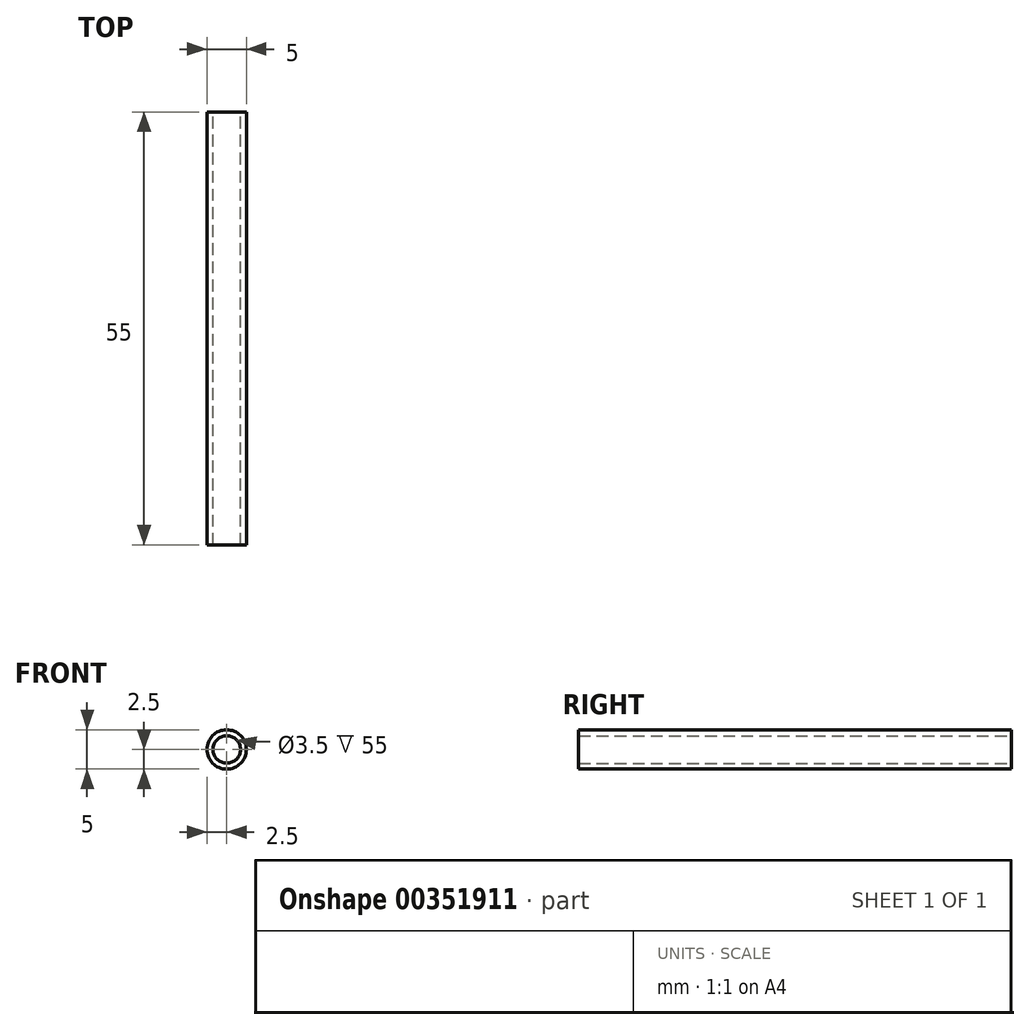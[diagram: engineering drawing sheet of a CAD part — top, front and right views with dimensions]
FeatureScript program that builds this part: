
annotation { "Feature Type Name" : "Feature", "Feature Type Description" : "" }
export const myFeature = defineFeature(function(context is Context, id is Id, definition is map)
    precondition{}
    {
        {
            var Q0;
            Q0=qCreatedBy(makeId("Front.planeOp"),FACE);
            var sketch = newSketch(context, id + "F0", { "sketchPlane" : qUnion([Q0])});
            skCircle(sketch, "E0", {"center": v(0, 0) * mm, "radius": 2.5 * mm});
            skCircle(sketch, "E1", {"center": v(0, 0) * mm, "radius": 1.75 * mm});
            skSolve(sketch);
        }
        {
            var Q0;
            Q0 = qSketchRegion(id + "F0", true);
            extrude(context, id + "F1", {"entities" : qUnion([Q0]), "depth" : 55 * mm});
        }
    });
